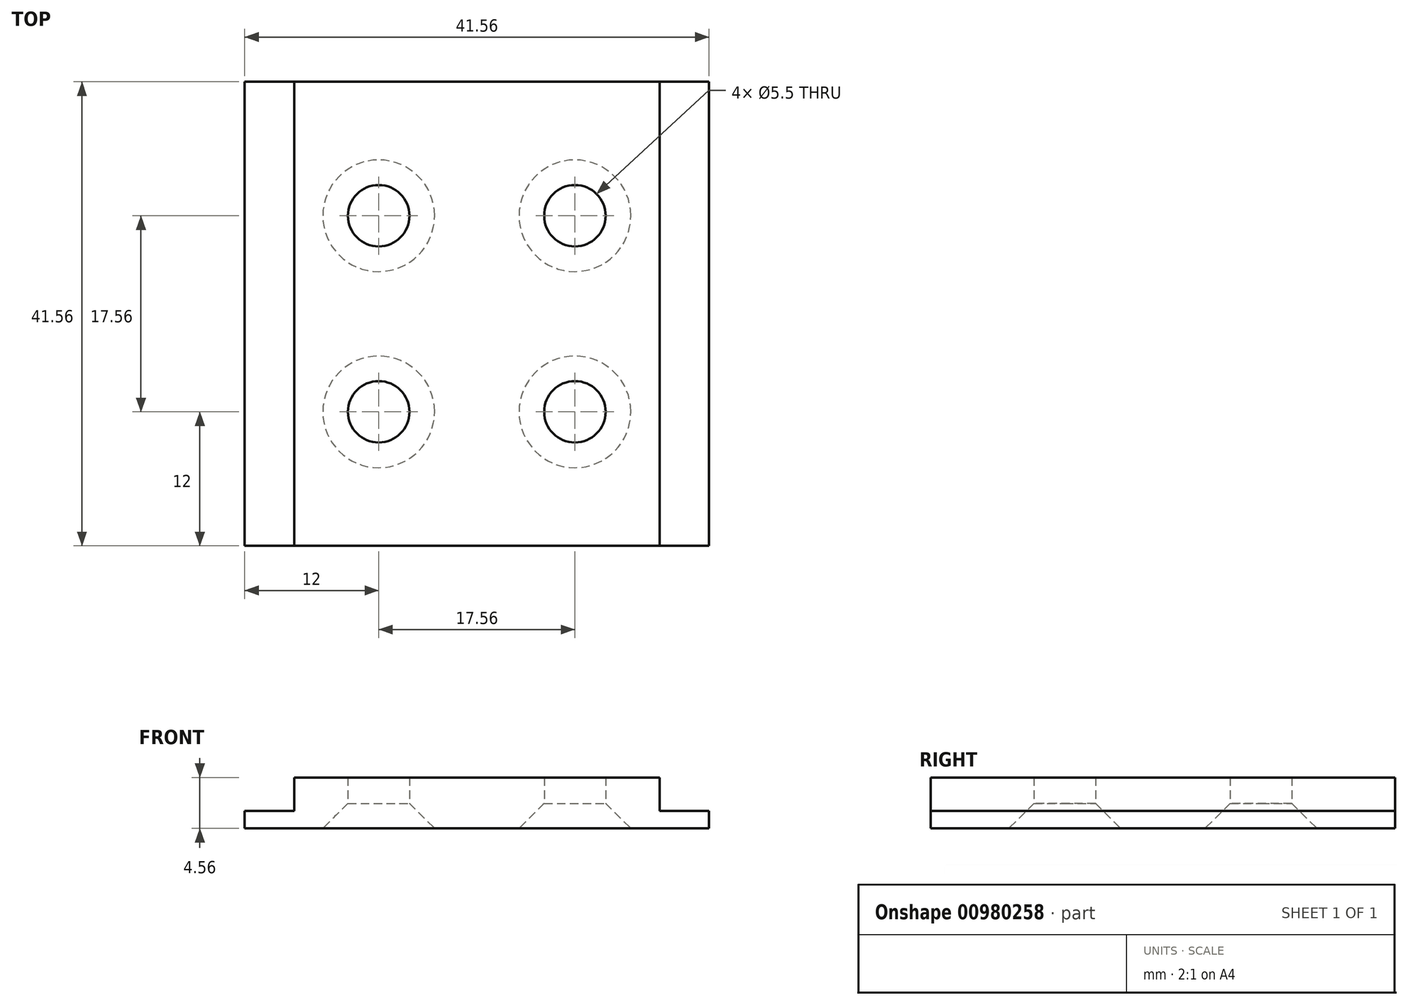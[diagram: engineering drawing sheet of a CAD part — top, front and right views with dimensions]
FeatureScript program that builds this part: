
annotation { "Feature Type Name" : "Feature", "Feature Type Description" : "" }
export const myFeature = defineFeature(function(context is Context, id is Id, definition is map)
    precondition{}
    {
        {
            var Q0;
            Q0=qCreatedBy(makeId("Top.planeOp"),FACE);
            var sketch = newSketch(context, id + "F0", { "sketchPlane" : qUnion([Q0])});
            skLineSegment(sketch, "E0.bottom", {"start": v(0, 0) * mm, "end": v(41.56, 0) * mm});
            skLineSegment(sketch, "E0.top", {"start": v(0, 41.56) * mm, "end": v(41.56, 41.56) * mm});
            skLineSegment(sketch, "E0.left", {"start": v(0, 0) * mm, "end": v(0, 41.56) * mm});
            skLineSegment(sketch, "E0.right", {"start": v(41.56, 0) * mm, "end": v(41.56, 41.56) * mm});
            skSolve(sketch);
        }
        {
            var Q0;
            Q0 = qSketchRegion(id + "F0", true);
            extrude(context, id + "F1", {"entities" : qUnion([Q0]), "depth" : 1.56 * mm, "offsetDistance" : 25 * mm});
        }
        {
            var Q0;
            Q0=makeQuery(id+"F1.opExtrude","CAP_FACE",FACE,{"disambiguationData":[OSD([sQuery(id+"F0.wireOp",EDGE,"E0.bottom"),sQuery(id+"F0.wireOp",EDGE,"E0.top"),sQuery(id+"F0.wireOp",EDGE,"E0.left"),sQuery(id+"F0.wireOp",EDGE,"E0.right")])],"isStart":false});
            var sketch = newSketch(context, id + "F2", { "sketchPlane" : qUnion([Q0])});
            skLineSegment(sketch, "E1.0", {"start": v(0, 41.56) * mm, "end": v(41.56, 41.56) * mm});
            skLineSegment(sketch, "E2.0", {"start": v(0, 0) * mm, "end": v(0, 41.56) * mm});
            skLineSegment(sketch, "E3.0", {"start": v(0, 0) * mm, "end": v(41.56, 0) * mm});
            skLineSegment(sketch, "E4.0", {"start": v(41.56, 0) * mm, "end": v(41.56, 41.56) * mm});
            skLineSegment(sketch, "E5", {"start": v(4.43, 41.56) * mm, "end": v(4.43, 0) * mm});
            skLineSegment(sketch, "E6", {"start": v(37.13, 41.56) * mm, "end": v(37.13, 0) * mm});
            skLineSegment(sketch, "E7", {"start": v(37.13, 20.78) * mm, "end": v(41.56, 20.78) * mm, "construction": true});
            skLineSegment(sketch, "E8", {"start": v(4.43, 20.78) * mm, "end": v(0, 20.78) * mm, "construction": true});
            skSolve(sketch);
        }
        {
            var Q0;
            {var subQ0=sQuery(id+"F2.wireOp",EDGE,"E5");Q0=makeQuery(id+"F2.imprint","IMPRINT",FACE,{"disambiguationData":[TD([[makeQuery(id+"F2.imprint","IMPRINT",EDGE,{"derivedFrom":subQ0}),1.0]])]});}
            extrude(context, id + "F3", {"entities" : qUnion([Q0]), "operationType" : NewBodyOperationType.ADD, "depth" : 3 * mm, "offsetDistance" : 25 * mm});
        }
        {
            var Q0;
            Q0=makeQuery(id+"F1.opExtrude","CAP_FACE",FACE,{"disambiguationData":[OSD([sQuery(id+"F0.wireOp",EDGE,"E0.bottom"),sQuery(id+"F0.wireOp",EDGE,"E0.top"),sQuery(id+"F0.wireOp",EDGE,"E0.left"),sQuery(id+"F0.wireOp",EDGE,"E0.right")])],"isStart":true});
            var sketch = newSketch(context, id + "F4", { "sketchPlane" : qUnion([Q0])});
            skLineSegment(sketch, "E9.0", {"start": v(0, 0) * mm, "end": v(41.56, 0) * mm});
            skLineSegment(sketch, "E10.0", {"start": v(41.56, 0) * mm, "end": v(41.56, -41.56) * mm});
            skPoint(sketch, "E10.1", {"position": v(41.56, -20.78) * mm});
            skLineSegment(sketch, "E11.0", {"start": v(0, -41.56) * mm, "end": v(41.56, -41.56) * mm});
            skLineSegment(sketch, "E12.0", {"start": v(0, 0) * mm, "end": v(0, -41.56) * mm});
            skLineSegment(sketch, "E13.0", {"start": v(12, -12) * mm, "end": v(29.56, -12) * mm, "construction": true});
            skLineSegment(sketch, "E13.1", {"start": v(12, -12) * mm, "end": v(12, -29.56) * mm, "construction": true});
            skLineSegment(sketch, "E13.2", {"start": v(12, -29.56) * mm, "end": v(29.56, -29.56) * mm, "construction": true});
            skLineSegment(sketch, "E13.3", {"start": v(29.56, -12) * mm, "end": v(29.56, -29.56) * mm, "construction": true});
            skSolve(sketch);
        }
        {
            var Q0;
            Q0=sQuery(id+"F4.wireOp",VERTEX,"E13.0.start");
            var Q1;
            Q1=sQuery(id+"F4.wireOp",VERTEX,"E13.0.end");
            var Q2;
            Q2=sQuery(id+"F4.wireOp",VERTEX,"E13.1.end");
            var Q3;
            Q3=sQuery(id+"F4.wireOp",VERTEX,"E13.2.end");
            var Q4;
            Q4=makeQuery(id+"F1.opExtrude","SWEPT_BODY",BODY,{"disambiguationData":[OSD([sQuery(id+"F0.wireOp",EDGE,"E0.bottom"),sQuery(id+"F0.wireOp",EDGE,"E0.top"),sQuery(id+"F0.wireOp",EDGE,"E0.left"),sQuery(id+"F0.wireOp",EDGE,"E0.right")])]});
            hole(context, id + "F5", {"style" : HoleStyle.C_SINK, "endStyle" : HoleEndStyle.BLIND, "holeDiameter" : 5.5 * mm, "cSinkDiameter" : 10 * mm, "cSinkAngle" : 90 * degree, "majorDiameter" : 5 * mm, "holeDepth" : 8 * mm, "isTappedThrough" : true, "tappedDepth" : 100 * mm, "tapClearance" : 3, "startFromSketch" : true, "locations" : qUnion([Q0, Q1, Q2, Q3]), "scope" : qUnion([Q4])});
        }
    });
